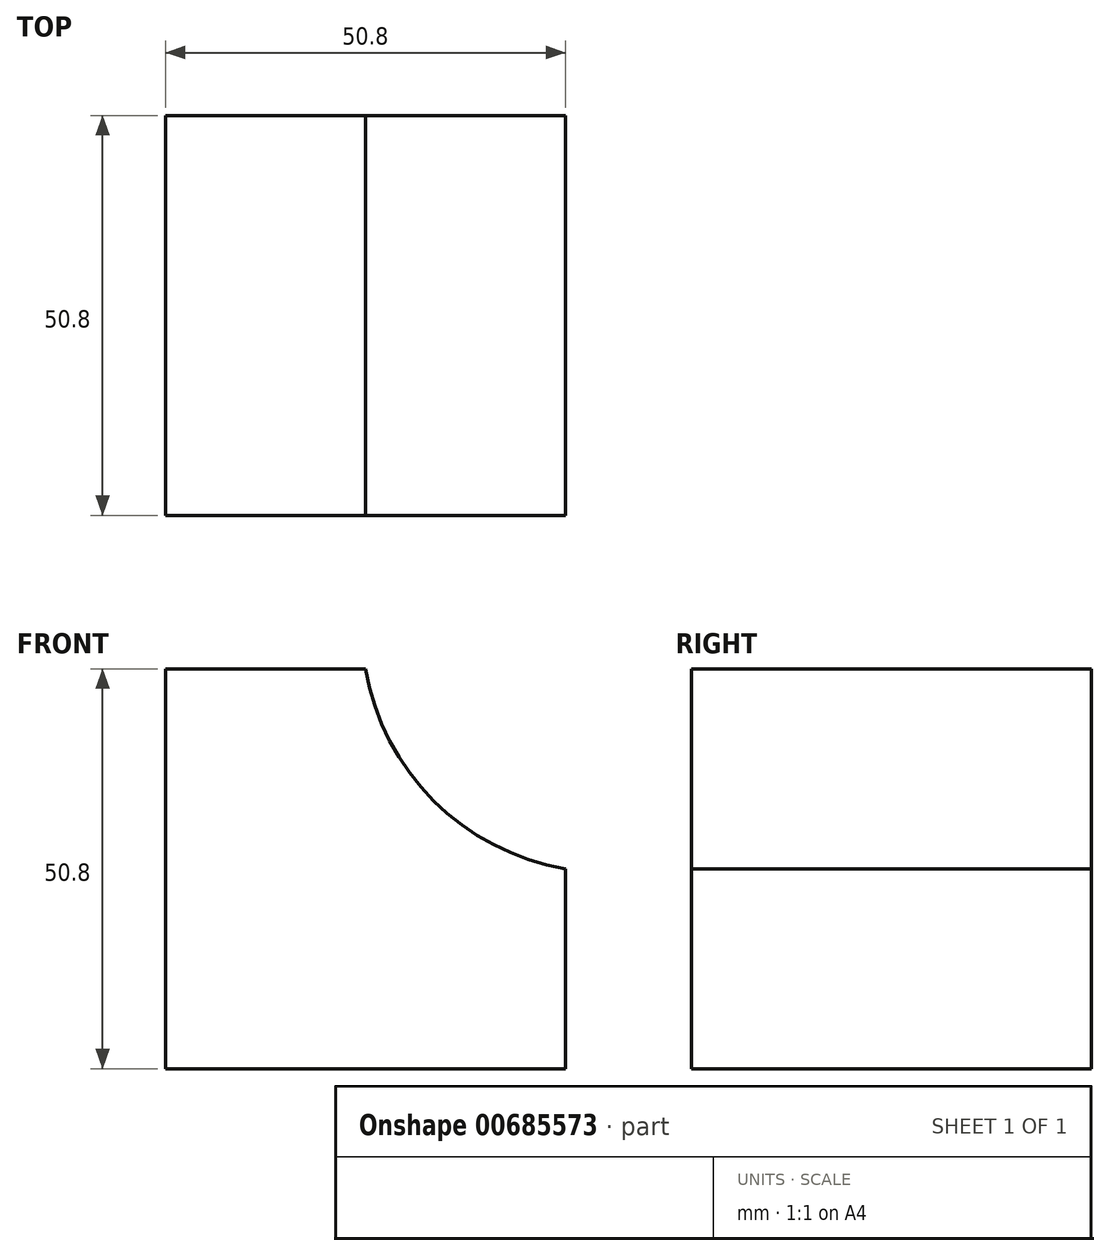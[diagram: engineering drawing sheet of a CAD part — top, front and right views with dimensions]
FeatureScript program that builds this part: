
annotation { "Feature Type Name" : "Feature", "Feature Type Description" : "" }
export const myFeature = defineFeature(function(context is Context, id is Id, definition is map)
    precondition{}
    {
        {
            var Q0;
            Q0=qCreatedBy(makeId("Front.planeOp"),FACE);
            var sketch = newSketch(context, id + "F0", { "sketchPlane" : qUnion([Q0])});
            skLineSegment(sketch, "E0", {"start": v(-11.3, 45.28) * mm, "end": v(-36.7, 45.28) * mm});
            skLineSegment(sketch, "E1", {"start": v(-36.7, 45.28) * mm, "end": v(-36.7, -5.52) * mm});
            skLineSegment(sketch, "E2", {"start": v(-36.7, -5.52) * mm, "end": v(14.1, -5.52) * mm});
            skLineSegment(sketch, "E3", {"start": v(14.1, -5.52) * mm, "end": v(14.1, 19.88) * mm});
            skArc(sketch, "E4", {"start": v(-11.3, 45.28) * mm, "mid": v(-2.66, 28.52) * mm, "end": v(14.1, 19.88) * mm});
            skSolve(sketch);
        }
        {
            var Q0;
            Q0 = qSketchRegion(id + "F0", true);
            extrude(context, id + "F1", {"entities" : qUnion([Q0]), "depth" : 50.8 * mm, "offsetDistance" : 25.4 * mm});
        }
    });
